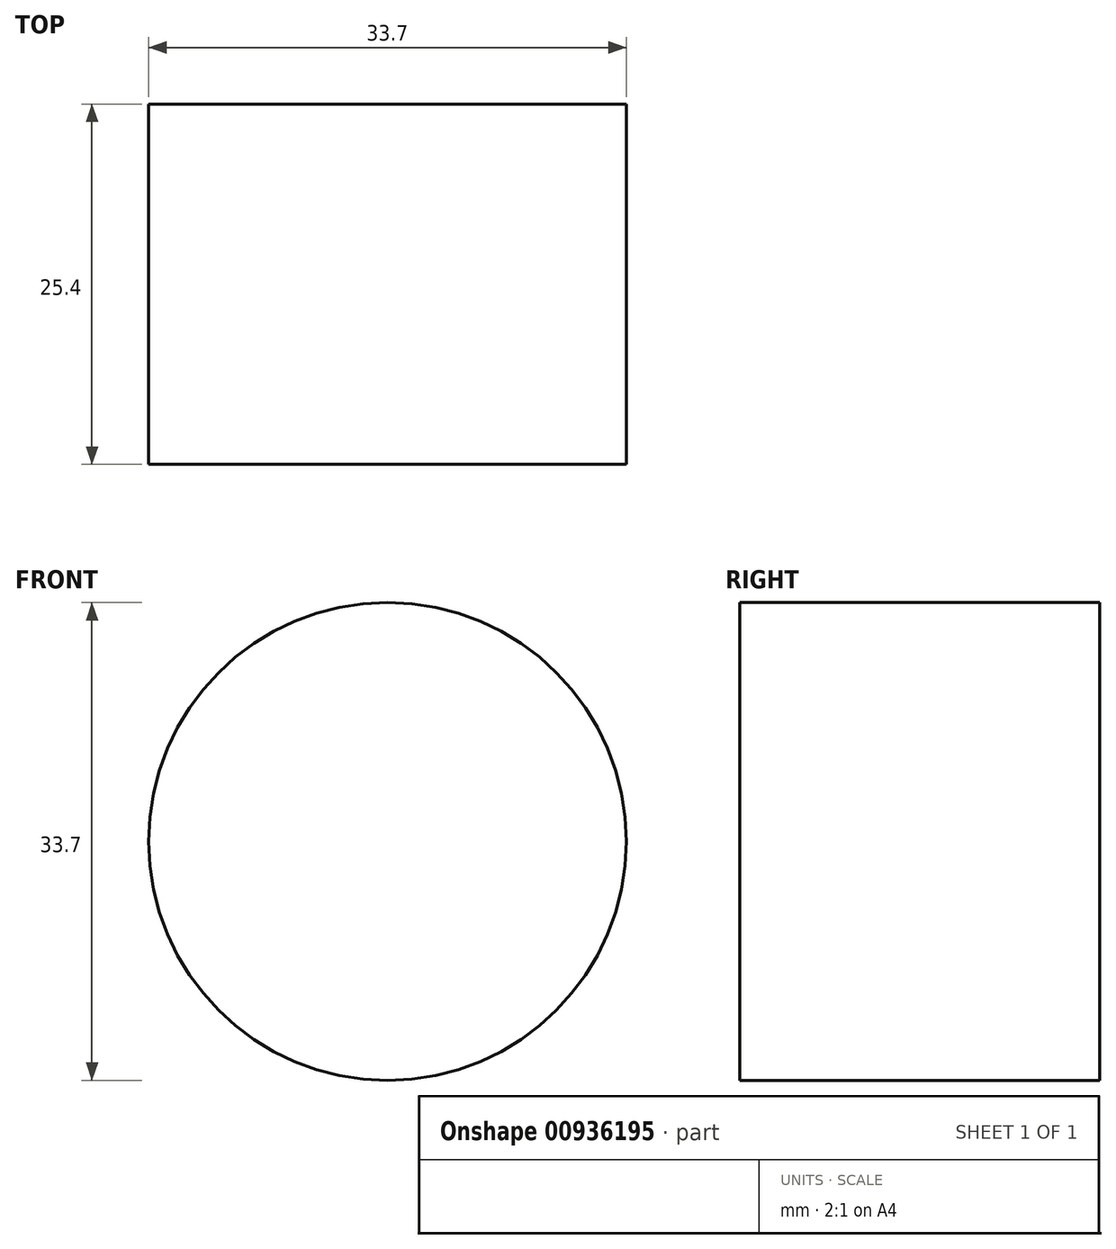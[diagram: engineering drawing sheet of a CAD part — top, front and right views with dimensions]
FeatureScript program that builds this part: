
annotation { "Feature Type Name" : "Feature", "Feature Type Description" : "" }
export const myFeature = defineFeature(function(context is Context, id is Id, definition is map)
    precondition{}
    {
        {
            var Q0;
            Q0=qCreatedBy(makeId("Front.planeOp"),FACE);
            var sketch = newSketch(context, id + "F0", { "sketchPlane" : qUnion([Q0])});
            skCircle(sketch, "E0", {"center": v(0, 0) * mm, "radius": 16.85 * mm});
            skSolve(sketch);
        }
        {
            var Q0;
            Q0=makeQuery(id+"F0.imprint","IMPRINT",FACE,{"disambiguationData":[TD([[makeQuery(id+"F0.imprint","IMPRINT",EDGE,{"derivedFrom":sQuery(id+"F0.wireOp",EDGE,"E0")}),1.0]])]});
            extrude(context, id + "F1", {"entities" : qUnion([Q0]), "depth" : 25.4 * mm, "offsetDistance" : 25.4 * mm});
        }
    });
